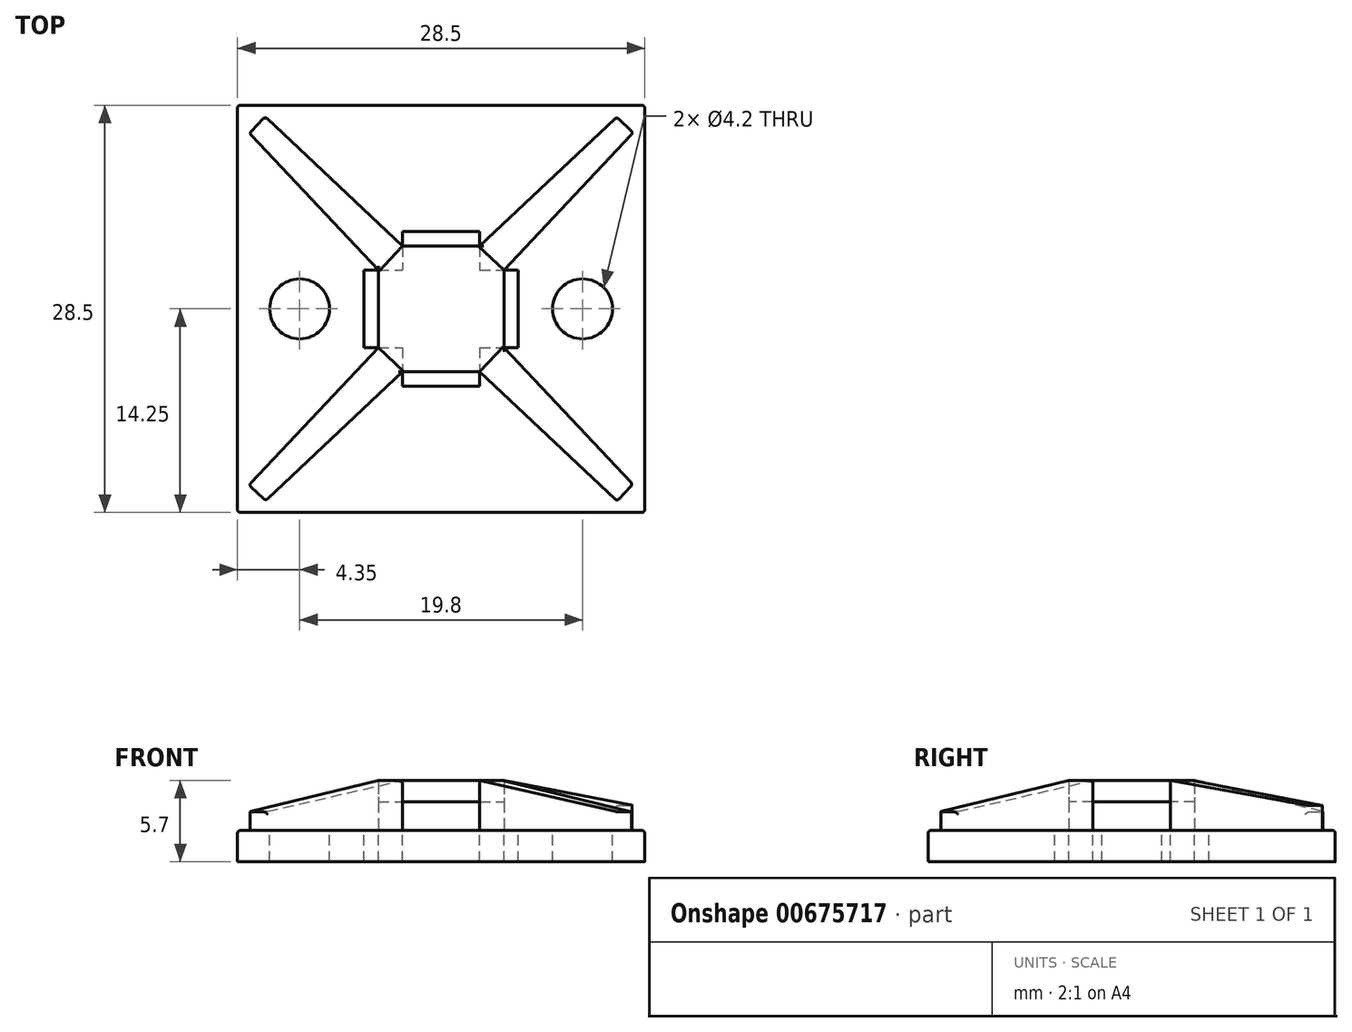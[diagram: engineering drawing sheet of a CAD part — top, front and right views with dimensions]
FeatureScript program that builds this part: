
annotation { "Feature Type Name" : "Feature", "Feature Type Description" : "" }
export const myFeature = defineFeature(function(context is Context, id is Id, definition is map)
    precondition{}
    {
        {
            var Q0;
            Q0=qCreatedBy(makeId("Top.planeOp"),FACE);
            var sketch = newSketch(context, id + "F0", { "sketchPlane" : qUnion([Q0])});
            skLineSegment(sketch, "E0.bottom", {"start": v(14.25, -14.25) * mm, "end": v(-14.25, -14.25) * mm});
            skLineSegment(sketch, "E0.top", {"start": v(14.25, 14.25) * mm, "end": v(-14.25, 14.25) * mm});
            skLineSegment(sketch, "E0.left", {"start": v(14.25, -14.25) * mm, "end": v(14.25, 14.25) * mm});
            skLineSegment(sketch, "E0.right", {"start": v(-14.25, -14.25) * mm, "end": v(-14.25, 14.25) * mm});
            skPoint(sketch, "E0.middle", {"position": v(0, 0) * mm});
            skSolve(sketch);
        }
        {
            var Q0;
            Q0 = qSketchRegion(id + "F0", true);
            extrude(context, id + "F1", {"entities" : qUnion([Q0]), "depth" : 2.2 * mm, "offsetDistance" : 25 * mm});
        }
        {
            var Q0;
            Q0=makeQuery(id+"F1.opExtrude","CAP_FACE",FACE,{"disambiguationData":[OSD([sQuery(id+"F0.wireOp",EDGE,"E0.bottom"),sQuery(id+"F0.wireOp",EDGE,"E0.top"),sQuery(id+"F0.wireOp",EDGE,"E0.left"),sQuery(id+"F0.wireOp",EDGE,"E0.right")])],"isStart":false});
            var sketch = newSketch(context, id + "F2", { "sketchPlane" : qUnion([Q0])});
            skPoint(sketch, "E1.middle", {"position": v(0, 0) * mm});
            skLineSegment(sketch, "E2", {"start": v(13.45, -12.32) * mm, "end": v(12.32, -13.45) * mm});
            skLineSegment(sketch, "E3", {"start": v(12.32, 13.45) * mm, "end": v(13.45, 12.32) * mm});
            skLineSegment(sketch, "E4.MirrorCS", {"start": v(-12.32, 13.45) * mm, "end": v(-13.45, 12.32) * mm});
            skLineSegment(sketch, "E5.MirrorCS", {"start": v(-13.45, -12.32) * mm, "end": v(-12.32, -13.45) * mm});
            skLineSegment(sketch, "E6", {"start": v(-4.4, 2.7) * mm, "end": v(-4.4, -2.7) * mm});
            skLineSegment(sketch, "E7", {"start": v(-2.7, -4.4) * mm, "end": v(2.7, -4.4) * mm});
            skLineSegment(sketch, "E8", {"start": v(4.4, -2.7) * mm, "end": v(4.4, 2.7) * mm});
            skLineSegment(sketch, "E9", {"start": v(2.7, 4.4) * mm, "end": v(-2.7, 4.4) * mm});
            skLineSegment(sketch, "E10", {"start": v(-13.45, 12.32) * mm, "end": v(-4.4, 2.7) * mm});
            skLineSegment(sketch, "E11", {"start": v(-12.32, 13.45) * mm, "end": v(-2.7, 4.4) * mm});
            skLineSegment(sketch, "E12", {"start": v(2.7, 4.4) * mm, "end": v(12.32, 13.45) * mm});
            skLineSegment(sketch, "E13", {"start": v(13.45, 12.32) * mm, "end": v(4.4, 2.7) * mm});
            skLineSegment(sketch, "E14", {"start": v(4.4, -2.7) * mm, "end": v(13.45, -12.32) * mm});
            skLineSegment(sketch, "E15", {"start": v(12.32, -13.45) * mm, "end": v(2.7, -4.4) * mm});
            skLineSegment(sketch, "E16", {"start": v(-2.7, -4.4) * mm, "end": v(-12.32, -13.45) * mm});
            skLineSegment(sketch, "E17", {"start": v(-13.45, -12.32) * mm, "end": v(-4.4, -2.7) * mm});
            skSolve(sketch);
        }
        {
            var Q0;
            Q0 = qSketchRegion(id + "F2", true);
            extrude(context, id + "F3", {"entities" : qUnion([Q0]), "operationType" : NewBodyOperationType.ADD, "depth" : 3.5 * mm, "offsetDistance" : 25 * mm});
        }
        {
            var Q0;
            Q0=makeQuery(id+"F3.opExtrude","SWEPT_FACE",FACE,{"disambiguationData":[OSD([sQuery(id+"F2.wireOp",EDGE,"E15")])]});
            var sketch = newSketch(context, id + "F4", { "sketchPlane" : qUnion([Q0])});
            skLineSegment(sketch, "E18", {"start": v(18.19, 3.5) * mm, "end": v(4.98, 5.7) * mm});
            skSolve(sketch);
        }
        {
            var Q0;
            Q0=makeQuery(id+"F3.opExtrude","SWEPT_FACE",FACE,{"disambiguationData":[OSD([sQuery(id+"F2.wireOp",EDGE,"E17")])]});
            var sketch = newSketch(context, id + "F5", { "sketchPlane" : qUnion([Q0])});
            skLineSegment(sketch, "E19", {"start": v(18.19, 3.5) * mm, "end": v(4.98, 5.7) * mm});
            skSolve(sketch);
        }
        {
            var Q0;
            Q0=makeQuery(id+"F3.opExtrude","SWEPT_FACE",FACE,{"disambiguationData":[OSD([sQuery(id+"F2.wireOp",EDGE,"E11")])]});
            var sketch = newSketch(context, id + "F6", { "sketchPlane" : qUnion([Q0])});
            skLineSegment(sketch, "E20", {"start": v(18.19, 3.5) * mm, "end": v(4.98, 5.7) * mm});
            skSolve(sketch);
        }
        {
            var Q0;
            Q0=makeQuery(id+"F3.opExtrude","SWEPT_FACE",FACE,{"disambiguationData":[OSD([sQuery(id+"F2.wireOp",EDGE,"E13")])]});
            var sketch = newSketch(context, id + "F7", { "sketchPlane" : qUnion([Q0])});
            skLineSegment(sketch, "E21", {"start": v(18.19, 3.95) * mm, "end": v(4.98, 5.7) * mm});
            skSolve(sketch);
        }
        {
            var Q0;
            {var subQ0=sQuery(id+"F7.wireOp",EDGE,"7hokAuO2-JDLf-I4zO-NzrR-DYuqV2taVxoO");Q0=makeQuery(id+"F7.imprint","IMPRINT",FACE,{"disambiguationData":[TD([[makeQuery(id+"F7.imprint","IMPRINT",EDGE,{"derivedFrom":subQ0}),1.0]])]});}
            var Q1;
            {var subQ0=sQuery(id+"F7.wireOp",EDGE,"E21");Q1=makeQuery(id+"F7.imprint","IMPRINT",FACE,{"disambiguationData":[TD([[makeQuery(id+"F7.imprint","IMPRINT",EDGE,{"derivedFrom":subQ0}),-1.0]])]});}
            var Q2;
            Q2=makeQuery(id+"F3.opExtrude","SWEPT_FACE",FACE,{"disambiguationData":[OSD([sQuery(id+"F2.wireOp",EDGE,"E3")])]});
            extrude(context, id + "F8", {"entities" : qUnion([Q0, Q1, Q2]), "operationType" : NewBodyOperationType.REMOVE, "endBound" : BoundingType.THROUGH_ALL, "oppositeDirection" : true, "depth" : 25 * mm, "offsetDistance" : 25 * mm});
        }
        {
            var Q0;
            {var subQ0=sQuery(id+"F6.wireOp",EDGE,"E20");Q0=makeQuery(id+"F6.imprint","IMPRINT",FACE,{"disambiguationData":[TD([[makeQuery(id+"F6.imprint","IMPRINT",EDGE,{"derivedFrom":subQ0}),-1.0]])]});}
            var Q1;
            Q1=makeQuery(id+"F3.opExtrude","SWEPT_FACE",FACE,{"disambiguationData":[OSD([sQuery(id+"F2.wireOp",EDGE,"E4.MirrorCS")])]});
            extrude(context, id + "F9", {"entities" : qUnion([Q0, Q1]), "operationType" : NewBodyOperationType.REMOVE, "endBound" : BoundingType.THROUGH_ALL, "oppositeDirection" : true, "depth" : 25 * mm, "offsetDistance" : 25 * mm});
        }
        {
            var Q0;
            {var subQ0=sQuery(id+"F5.wireOp",EDGE,"E19");Q0=makeQuery(id+"F5.imprint","IMPRINT",FACE,{"disambiguationData":[TD([[makeQuery(id+"F5.imprint","IMPRINT",EDGE,{"derivedFrom":subQ0}),-1.0]])]});}
            var Q1;
            Q1=makeQuery(id+"F3.opExtrude","SWEPT_FACE",FACE,{"disambiguationData":[OSD([sQuery(id+"F2.wireOp",EDGE,"E5.MirrorCS")])]});
            extrude(context, id + "F10", {"entities" : qUnion([Q0, Q1]), "operationType" : NewBodyOperationType.REMOVE, "endBound" : BoundingType.THROUGH_ALL, "oppositeDirection" : true, "depth" : 25 * mm, "offsetDistance" : 25 * mm});
        }
        {
            var Q0;
            {var subQ0=sQuery(id+"F4.wireOp",EDGE,"E18");Q0=makeQuery(id+"F4.imprint","IMPRINT",FACE,{"disambiguationData":[TD([[makeQuery(id+"F4.imprint","IMPRINT",EDGE,{"derivedFrom":subQ0}),-1.0]])]});}
            var Q1;
            Q1=makeQuery(id+"F3.opExtrude","SWEPT_FACE",FACE,{"disambiguationData":[OSD([sQuery(id+"F2.wireOp",EDGE,"E2")])]});
            extrude(context, id + "F11", {"entities" : qUnion([Q0, Q1]), "operationType" : NewBodyOperationType.REMOVE, "endBound" : BoundingType.THROUGH_ALL, "oppositeDirection" : true, "depth" : 25 * mm, "offsetDistance" : 25 * mm});
        }
        {
            var Q0;
            {var subQ0=sQuery(id+"F2.wireOp",EDGE,"E2");var subQ1=sQuery(id+"F2.wireOp",EDGE,"E5.MirrorCS");var subQ2=sQuery(id+"F2.wireOp",EDGE,"E4.MirrorCS");var subQ3=sQuery(id+"F2.wireOp",EDGE,"E3");Q0=makeQuery(id+"F11.boolean.opBoolean","MERGE",FACE,{"derivedFrom":[makeQuery(id+"F10.boolean.opBoolean","MERGE",FACE,{"derivedFrom":[makeQuery(id+"F9.boolean.opBoolean","MERGE",FACE,{"derivedFrom":[makeQuery(id+"F8.boolean.opBoolean","MERGE",FACE,{"derivedFrom":[makeQuery(id+"F1.opExtrude","CAP_FACE",FACE,{"disambiguationData":[OSD([sQuery(id+"F0.wireOp",EDGE,"E0.bottom"),sQuery(id+"F0.wireOp",EDGE,"E0.top"),sQuery(id+"F0.wireOp",EDGE,"E0.left"),sQuery(id+"F0.wireOp",EDGE,"E0.right")])],"isStart":false}),makeQuery(id+"F8.opExtrude","SWEPT_FACE",FACE,{"disambiguationData":[OSD([subQ3]),TDD([makeQuery(id+"F3.opExtrude","CAP_EDGE",EDGE,{"disambiguationData":[OSD([subQ3])],"isStart":true})])]})]}),makeQuery(id+"F9.opExtrude","SWEPT_FACE",FACE,{"disambiguationData":[OSD([subQ2]),TDD([makeQuery(id+"F3.opExtrude","CAP_EDGE",EDGE,{"disambiguationData":[OSD([subQ2])],"isStart":true})])]})]}),makeQuery(id+"F10.opExtrude","SWEPT_FACE",FACE,{"disambiguationData":[OSD([subQ1]),TDD([makeQuery(id+"F3.opExtrude","CAP_EDGE",EDGE,{"disambiguationData":[OSD([subQ1])],"isStart":true})])]})]}),makeQuery(id+"F11.opExtrude","SWEPT_FACE",FACE,{"disambiguationData":[OSD([subQ0]),TDD([makeQuery(id+"F3.opExtrude","CAP_EDGE",EDGE,{"disambiguationData":[OSD([subQ0])],"isStart":true})])]})]});}
            var sketch = newSketch(context, id + "F12", { "sketchPlane" : qUnion([Q0])});
            skCircle(sketch, "E22", {"center": v(-9.9, 0) * mm, "radius": 2.1 * mm});
            skCircle(sketch, "E23", {"center": v(9.9, 0) * mm, "radius": 2.1 * mm});
            skLineSegment(sketch, "E24", {"start": v(2.7, 5.4) * mm, "end": v(2.7, 4.4) * mm});
            skLineSegment(sketch, "E25", {"start": v(2.7, 4.4) * mm, "end": v(-2.7, 4.4) * mm});
            skLineSegment(sketch, "E26", {"start": v(-2.7, 4.4) * mm, "end": v(-2.7, 5.4) * mm});
            skLineSegment(sketch, "E27", {"start": v(-2.7, 5.4) * mm, "end": v(2.7, 5.4) * mm});
            skLineSegment(sketch, "E28", {"start": v(-4.4, 2.7) * mm, "end": v(-5.4, 2.7) * mm});
            skLineSegment(sketch, "E29", {"start": v(-5.4, 2.7) * mm, "end": v(-5.4, -2.7) * mm});
            skLineSegment(sketch, "E30", {"start": v(-5.4, -2.7) * mm, "end": v(-4.4, -2.7) * mm});
            skLineSegment(sketch, "E31", {"start": v(-4.4, -2.7) * mm, "end": v(-4.4, 2.56) * mm});
            skLineSegment(sketch, "E32.MirrorCS", {"start": v(4.4, -2.7) * mm, "end": v(4.4, 2.56) * mm});
            skLineSegment(sketch, "E33.MirrorCS", {"start": v(5.4, -2.7) * mm, "end": v(4.4, -2.7) * mm});
            skLineSegment(sketch, "E34.MirrorCS", {"start": v(4.4, 2.7) * mm, "end": v(5.4, 2.7) * mm});
            skLineSegment(sketch, "E35.MirrorCS", {"start": v(5.4, 2.7) * mm, "end": v(5.4, -2.7) * mm});
            skLineSegment(sketch, "E36.MirrorCS", {"start": v(-2.7, -4.4) * mm, "end": v(-2.7, -5.4) * mm});
            skLineSegment(sketch, "E37.MirrorCS", {"start": v(-2.7, -5.4) * mm, "end": v(2.7, -5.4) * mm});
            skLineSegment(sketch, "E38.MirrorCS", {"start": v(2.7, -5.4) * mm, "end": v(2.7, -4.4) * mm});
            skLineSegment(sketch, "E39.MirrorCS", {"start": v(2.7, -4.4) * mm, "end": v(-2.7, -4.4) * mm});
            skSolve(sketch);
        }
        {
            var Q0;
            Q0 = qSketchRegion(id + "F12", true);
            var Q1;
            {var subQ1=sQuery(id+"F12.wireOp",EDGE,"E28");Q1=makeQuery(id+"F12.imprint","IMPRINT",FACE,{"disambiguationData":[TD([[makeQuery(id+"F12.imprint","IMPRINT",EDGE,{"derivedFrom":subQ1}),1.0]])]});}
            var Q2;
            {var subQ1=sQuery(id+"F12.wireOp",EDGE,"E32.MirrorCS");Q2=makeQuery(id+"F12.imprint","IMPRINT",FACE,{"disambiguationData":[TD([[makeQuery(id+"F12.imprint","IMPRINT",EDGE,{"derivedFrom":subQ1}),-1.0]])]});}
            extrude(context, id + "F13", {"entities" : qUnion([Q0, Q1, Q2]), "operationType" : NewBodyOperationType.REMOVE, "endBound" : BoundingType.THROUGH_ALL, "oppositeDirection" : true, "depth" : 25 * mm, "offsetDistance" : 25 * mm});
        }
        {
            var Q0;
            Q0=makeQuery(id+"F13.boolean.opBoolean","MERGE",FACE,{"derivedFrom":[makeQuery(id+"F3.opExtrude","SWEPT_FACE",FACE,{"disambiguationData":[OSD([sQuery(id+"F2.wireOp",EDGE,"E7")])]}),makeQuery(id+"F13.opExtrude","SWEPT_FACE",FACE,{"disambiguationData":[OSD([sQuery(id+"F12.wireOp",EDGE,"E39.MirrorCS")])]})]});
            var sketch = newSketch(context, id + "F14", { "sketchPlane" : qUnion([Q0])});
            skLineSegment(sketch, "E40.bottom", {"start": v(2.7, 2.2) * mm, "end": v(-2.7, 2.2) * mm});
            skLineSegment(sketch, "E40.top", {"start": v(2.7, 4.2) * mm, "end": v(-2.7, 4.2) * mm});
            skLineSegment(sketch, "E40.left", {"start": v(2.7, 2.2) * mm, "end": v(2.7, 4.2) * mm});
            skLineSegment(sketch, "E40.right", {"start": v(-2.7, 2.2) * mm, "end": v(-2.7, 4.2) * mm});
            skPoint(sketch, "E40.middle", {"position": v(0, 3.2) * mm});
            skSolve(sketch);
        }
        {
            var Q0;
            {var subQ0=sQuery(id+"F2.wireOp",EDGE,"E8");Q0=makeQuery(id+"F13.boolean.opBoolean","MERGE",FACE,{"derivedFrom":[makeQuery(id+"F3.opExtrude","SWEPT_FACE",FACE,{"disambiguationData":[OSD([subQ0])]}),makeQuery(id+"F13.opExtrude","SWEPT_FACE",FACE,{"disambiguationData":[OSD([subQ0,sQuery(id+"F12.wireOp",EDGE,"E32.MirrorCS")])]})]});}
            var sketch = newSketch(context, id + "F15", { "sketchPlane" : qUnion([Q0])});
            skLineSegment(sketch, "E41.bottom", {"start": v(2.7, 2.2) * mm, "end": v(-2.7, 2.2) * mm});
            skLineSegment(sketch, "E41.top", {"start": v(2.7, 4.2) * mm, "end": v(-2.7, 4.2) * mm});
            skLineSegment(sketch, "E41.left", {"start": v(2.7, 2.2) * mm, "end": v(2.7, 4.2) * mm});
            skLineSegment(sketch, "E41.right", {"start": v(-2.7, 2.2) * mm, "end": v(-2.7, 4.2) * mm});
            skPoint(sketch, "E41.middle", {"position": v(0, 3.2) * mm});
            skSolve(sketch);
        }
        {
            var Q0;
            Q0=makeQuery(id+"F14.imprint","IMPRINT",FACE,{"disambiguationData":[TD([[makeQuery(id+"F14.imprint","IMPRINT",EDGE,{"derivedFrom":sQuery(id+"F14.wireOp",EDGE,"E40.bottom")}),-1.0]])]});
            extrude(context, id + "F16", {"entities" : qUnion([Q0]), "operationType" : NewBodyOperationType.REMOVE, "endBound" : BoundingType.THROUGH_ALL, "oppositeDirection" : true, "depth" : 25 * mm, "offsetDistance" : 25 * mm});
        }
        {
            var Q0;
            Q0=makeQuery(id+"F15.imprint","IMPRINT",FACE,{"disambiguationData":[TD([[makeQuery(id+"F15.imprint","IMPRINT",EDGE,{"derivedFrom":sQuery(id+"F15.wireOp",EDGE,"E41.bottom")}),-1.0]])]});
            extrude(context, id + "F17", {"entities" : qUnion([Q0]), "operationType" : NewBodyOperationType.REMOVE, "endBound" : BoundingType.THROUGH_ALL, "oppositeDirection" : true, "depth" : 25 * mm, "offsetDistance" : 25 * mm});
        }
        {
            var Q0;
            Q0=makeQuery(id+"F10.boolean.opBoolean","COPY",EDGE,{"derivedFrom":makeQuery(id+"F10.opExtrude","CAP_EDGE",EDGE,{"disambiguationData":[OSD([sQuery(id+"F5.wireOp",EDGE,"E19")])],"isStart":true})});
            var Q1;
            Q1=makeQuery(id+"F10.boolean.opBoolean","COPY",EDGE,{"derivedFrom":makeQuery(id+"F10.opExtrude","SWEPT_EDGE",EDGE,{"disambiguationData":[OSD([sQuery(id+"F2.wireOp",EDGE,"E5.MirrorCS"),sQuery(id+"F2.wireOp",EDGE,"E17"),sQuery(id+"F5.wireOp",EDGE,"E19")])]})});
            var Q2;
            Q2=makeQuery(id+"F10.boolean.opBoolean","INTERSECT",EDGE,{"derivedFrom":[makeQuery(id+"F3.opExtrude","SWEPT_FACE",FACE,{"disambiguationData":[OSD([sQuery(id+"F2.wireOp",EDGE,"E16")])]}),makeQuery(id+"F10.opExtrude","SWEPT_FACE",FACE,{"disambiguationData":[OSD([sQuery(id+"F5.wireOp",EDGE,"E19")])]})]});
            var Q3;
            Q3=makeQuery(id+"F11.boolean.opBoolean","COPY",EDGE,{"derivedFrom":makeQuery(id+"F11.opExtrude","CAP_EDGE",EDGE,{"disambiguationData":[OSD([sQuery(id+"F4.wireOp",EDGE,"E18")])],"isStart":true})});
            var Q4;
            Q4=makeQuery(id+"F11.boolean.opBoolean","COPY",EDGE,{"derivedFrom":makeQuery(id+"F11.opExtrude","SWEPT_EDGE",EDGE,{"disambiguationData":[OSD([sQuery(id+"F2.wireOp",EDGE,"E2"),sQuery(id+"F2.wireOp",EDGE,"E15"),sQuery(id+"F4.wireOp",EDGE,"E18")])]})});
            var Q5;
            Q5=makeQuery(id+"F11.boolean.opBoolean","INTERSECT",EDGE,{"derivedFrom":[makeQuery(id+"F3.opExtrude","SWEPT_FACE",FACE,{"disambiguationData":[OSD([sQuery(id+"F2.wireOp",EDGE,"E14")])]}),makeQuery(id+"F11.opExtrude","SWEPT_FACE",FACE,{"disambiguationData":[OSD([sQuery(id+"F4.wireOp",EDGE,"E18")])]})]});
            var Q6;
            {var subQ0=sQuery(id+"F2.wireOp",EDGE,"E15");var subQ1=sQuery(id+"F2.wireOp",EDGE,"E2");Q6=makeQuery(id+"F11.boolean.opBoolean","INTERSECT",EDGE,{"derivedFrom":[makeQuery(id+"F3.opExtrude","SWEPT_FACE",FACE,{"disambiguationData":[OSD([sQuery(id+"F2.wireOp",EDGE,"E14")])]}),makeQuery(id+"F11.opExtrude","SWEPT_FACE",FACE,{"disambiguationData":[OSD([subQ1,subQ0]),TDD([makeQuery(id+"F3.opExtrude","SWEPT_EDGE",EDGE,{"disambiguationData":[OSD([subQ1,subQ0])]})])]})]});}
            var Q7;
            {var subQ0=sQuery(id+"F2.wireOp",EDGE,"E15");var subQ1=sQuery(id+"F2.wireOp",EDGE,"E2");var subQ2=makeQuery(id+"F3.opExtrude","SWEPT_EDGE",EDGE,{"disambiguationData":[OSD([subQ1,subQ0])]});Q7=makeQuery(id+"F11.boolean.opBoolean","MERGE",EDGE,{"derivedFrom":[subQ2,makeQuery(id+"F11.opExtrude","CAP_EDGE",EDGE,{"disambiguationData":[OSD([subQ1,subQ0]),TDD([subQ2]),OD(0.0)],"isStart":false})]});}
            var Q8;
            {var subQ0=sQuery(id+"F2.wireOp",EDGE,"E17");var subQ1=sQuery(id+"F2.wireOp",EDGE,"E5.MirrorCS");var subQ2=makeQuery(id+"F3.opExtrude","SWEPT_EDGE",EDGE,{"disambiguationData":[OSD([subQ1,subQ0])]});Q8=makeQuery(id+"F10.boolean.opBoolean","MERGE",EDGE,{"derivedFrom":[subQ2,makeQuery(id+"F10.opExtrude","CAP_EDGE",EDGE,{"disambiguationData":[OSD([subQ1,subQ0]),TDD([subQ2]),OD(0.0)],"isStart":false})]});}
            var Q9;
            {var subQ0=sQuery(id+"F2.wireOp",EDGE,"E17");var subQ1=sQuery(id+"F2.wireOp",EDGE,"E5.MirrorCS");Q9=makeQuery(id+"F10.boolean.opBoolean","INTERSECT",EDGE,{"derivedFrom":[makeQuery(id+"F3.opExtrude","SWEPT_FACE",FACE,{"disambiguationData":[OSD([sQuery(id+"F2.wireOp",EDGE,"E16")])]}),makeQuery(id+"F10.opExtrude","SWEPT_FACE",FACE,{"disambiguationData":[OSD([subQ1,subQ0]),TDD([makeQuery(id+"F3.opExtrude","SWEPT_EDGE",EDGE,{"disambiguationData":[OSD([subQ1,subQ0])]})])]})]});}
            var Q10;
            Q10=makeQuery(id+"F9.boolean.opBoolean","INTERSECT",EDGE,{"derivedFrom":[makeQuery(id+"F3.opExtrude","SWEPT_FACE",FACE,{"disambiguationData":[OSD([sQuery(id+"F2.wireOp",EDGE,"E10")])]}),makeQuery(id+"F9.opExtrude","SWEPT_FACE",FACE,{"disambiguationData":[OSD([sQuery(id+"F6.wireOp",EDGE,"E20")])]})]});
            var Q11;
            Q11=makeQuery(id+"F9.boolean.opBoolean","COPY",EDGE,{"derivedFrom":makeQuery(id+"F9.opExtrude","CAP_EDGE",EDGE,{"disambiguationData":[OSD([sQuery(id+"F6.wireOp",EDGE,"E20")])],"isStart":true})});
            var Q12;
            Q12=makeQuery(id+"F9.boolean.opBoolean","COPY",EDGE,{"derivedFrom":makeQuery(id+"F9.opExtrude","SWEPT_EDGE",EDGE,{"disambiguationData":[OSD([sQuery(id+"F2.wireOp",EDGE,"E4.MirrorCS"),sQuery(id+"F2.wireOp",EDGE,"E11"),sQuery(id+"F6.wireOp",EDGE,"E20")])]})});
            var Q13;
            {var subQ0=sQuery(id+"F2.wireOp",EDGE,"E11");var subQ1=sQuery(id+"F2.wireOp",EDGE,"E4.MirrorCS");var subQ2=makeQuery(id+"F3.opExtrude","SWEPT_EDGE",EDGE,{"disambiguationData":[OSD([subQ1,subQ0])]});Q13=makeQuery(id+"F9.boolean.opBoolean","MERGE",EDGE,{"derivedFrom":[subQ2,makeQuery(id+"F9.opExtrude","CAP_EDGE",EDGE,{"disambiguationData":[OSD([subQ1,subQ0]),TDD([subQ2]),OD(1.0)],"isStart":false})]});}
            var Q14;
            {var subQ0=sQuery(id+"F2.wireOp",EDGE,"E11");var subQ1=sQuery(id+"F2.wireOp",EDGE,"E4.MirrorCS");Q14=makeQuery(id+"F9.boolean.opBoolean","INTERSECT",EDGE,{"derivedFrom":[makeQuery(id+"F3.opExtrude","SWEPT_FACE",FACE,{"disambiguationData":[OSD([sQuery(id+"F2.wireOp",EDGE,"E10")])]}),makeQuery(id+"F9.opExtrude","SWEPT_FACE",FACE,{"disambiguationData":[OSD([subQ1,subQ0]),TDD([makeQuery(id+"F3.opExtrude","SWEPT_EDGE",EDGE,{"disambiguationData":[OSD([subQ1,subQ0])]})])]})]});}
            var Q15;
            Q15=makeQuery(id+"F8.boolean.opBoolean","COPY",EDGE,{"derivedFrom":makeQuery(id+"F8.opExtrude","CAP_EDGE",EDGE,{"disambiguationData":[OSD([sQuery(id+"F7.wireOp",EDGE,"E21")])],"isStart":true})});
            var Q16;
            Q16=makeQuery(id+"F8.boolean.opBoolean","INTERSECT",EDGE,{"derivedFrom":[makeQuery(id+"F3.opExtrude","SWEPT_FACE",FACE,{"disambiguationData":[OSD([sQuery(id+"F2.wireOp",EDGE,"E12")])]}),makeQuery(id+"F8.opExtrude","SWEPT_FACE",FACE,{"disambiguationData":[OSD([sQuery(id+"F7.wireOp",EDGE,"E21")])]})]});
            var Q17;
            Q17=makeQuery(id+"F8.boolean.opBoolean","COPY",EDGE,{"derivedFrom":makeQuery(id+"F8.opExtrude","SWEPT_EDGE",EDGE,{"disambiguationData":[OSD([sQuery(id+"F2.wireOp",EDGE,"E3"),sQuery(id+"F2.wireOp",EDGE,"E13"),sQuery(id+"F7.wireOp",EDGE,"E21")])]})});
            var Q18;
            {var subQ0=sQuery(id+"F2.wireOp",EDGE,"E13");var subQ1=sQuery(id+"F2.wireOp",EDGE,"E3");var subQ2=makeQuery(id+"F3.opExtrude","SWEPT_EDGE",EDGE,{"disambiguationData":[OSD([subQ1,subQ0])]});Q18=makeQuery(id+"F8.boolean.opBoolean","MERGE",EDGE,{"derivedFrom":[subQ2,makeQuery(id+"F8.opExtrude","CAP_EDGE",EDGE,{"disambiguationData":[OSD([subQ1,subQ0]),TDD([subQ2]),OD(1.0)],"isStart":false})]});}
            var Q19;
            {var subQ0=sQuery(id+"F2.wireOp",EDGE,"E13");var subQ1=sQuery(id+"F2.wireOp",EDGE,"E3");Q19=makeQuery(id+"F8.boolean.opBoolean","INTERSECT",EDGE,{"derivedFrom":[makeQuery(id+"F3.opExtrude","SWEPT_FACE",FACE,{"disambiguationData":[OSD([sQuery(id+"F2.wireOp",EDGE,"E12")])]}),makeQuery(id+"F8.opExtrude","SWEPT_FACE",FACE,{"disambiguationData":[OSD([subQ1,subQ0]),TDD([makeQuery(id+"F3.opExtrude","SWEPT_EDGE",EDGE,{"disambiguationData":[OSD([subQ1,subQ0])]})])]})]});}
            var Q20;
            Q20=makeQuery(id+"F1.opExtrude","CAP_EDGE",EDGE,{"disambiguationData":[OSD([sQuery(id+"F0.wireOp",EDGE,"E0.top")])],"isStart":false});
            var Q21;
            Q21=makeQuery(id+"F1.opExtrude","SWEPT_EDGE",EDGE,{"disambiguationData":[OSD([sQuery(id+"F0.wireOp",EDGE,"E0.top"),sQuery(id+"F0.wireOp",EDGE,"E0.right")])]});
            var Q22;
            Q22=makeQuery(id+"F1.opExtrude","CAP_EDGE",EDGE,{"disambiguationData":[OSD([sQuery(id+"F0.wireOp",EDGE,"E0.right")])],"isStart":false});
            var Q23;
            Q23=makeQuery(id+"F1.opExtrude","SWEPT_EDGE",EDGE,{"disambiguationData":[OSD([sQuery(id+"F0.wireOp",EDGE,"E0.top"),sQuery(id+"F0.wireOp",EDGE,"E0.left")])]});
            var Q24;
            Q24=makeQuery(id+"F1.opExtrude","CAP_EDGE",EDGE,{"disambiguationData":[OSD([sQuery(id+"F0.wireOp",EDGE,"E0.left")])],"isStart":false});
            var Q25;
            Q25=makeQuery(id+"F1.opExtrude","SWEPT_EDGE",EDGE,{"disambiguationData":[OSD([sQuery(id+"F0.wireOp",EDGE,"E0.bottom"),sQuery(id+"F0.wireOp",EDGE,"E0.left")])]});
            var Q26;
            Q26=makeQuery(id+"F1.opExtrude","CAP_EDGE",EDGE,{"disambiguationData":[OSD([sQuery(id+"F0.wireOp",EDGE,"E0.bottom")])],"isStart":false});
            var Q27;
            Q27=makeQuery(id+"F1.opExtrude","SWEPT_EDGE",EDGE,{"disambiguationData":[OSD([sQuery(id+"F0.wireOp",EDGE,"E0.bottom"),sQuery(id+"F0.wireOp",EDGE,"E0.right")])]});
            fillet(context, id + "F18", {"entities" : qUnion([Q0, Q1, Q2, Q3, Q4, Q5, Q6, Q7, Q8, Q9, Q10, Q11, Q12, Q13, Q14, Q15, Q16, Q17, Q18, Q19, Q20, Q21, Q22, Q23, Q24, Q25, Q26, Q27]), "radius" : .2 * mm, "tangentPropagation" : true, "allowEdgeOverflow" : false});
        }
    });
